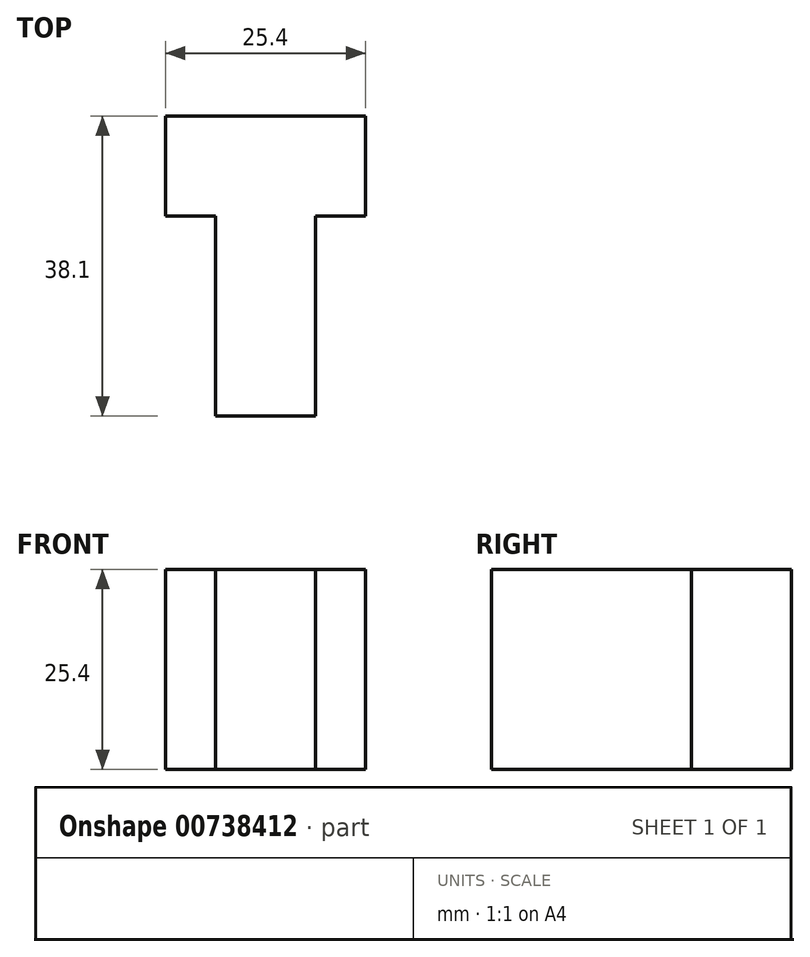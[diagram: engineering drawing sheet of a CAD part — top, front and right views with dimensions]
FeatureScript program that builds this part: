
annotation { "Feature Type Name" : "Feature", "Feature Type Description" : "" }
export const myFeature = defineFeature(function(context is Context, id is Id, definition is map)
    precondition{}
    {
        {
            var Q0;
            Q0=qCreatedBy(makeId("Top.planeOp"),FACE);
            var sketch = newSketch(context, id + "F0", { "sketchPlane" : qUnion([Q0])});
            skLineSegment(sketch, "E0", {"start": v(0, 17.79) * mm, "end": v(0, -7.61) * mm});
            skLineSegment(sketch, "E1", {"start": v(0, -7.61) * mm, "end": v(12.7, -7.61) * mm});
            skLineSegment(sketch, "E2", {"start": v(12.7, -7.61) * mm, "end": v(12.7, 17.79) * mm});
            skLineSegment(sketch, "E3", {"start": v(12.7, 17.79) * mm, "end": v(19.05, 17.79) * mm});
            skLineSegment(sketch, "E4", {"start": v(19.05, 17.79) * mm, "end": v(19.05, 30.49) * mm});
            skLineSegment(sketch, "E5", {"start": v(19.05, 30.49) * mm, "end": v(-6.35, 30.49) * mm});
            skLineSegment(sketch, "E6", {"start": v(-6.35, 30.49) * mm, "end": v(-6.35, 17.79) * mm});
            skLineSegment(sketch, "E7", {"start": v(-6.35, 17.79) * mm, "end": v(0, 17.79) * mm});
            skSolve(sketch);
        }
        {
            var Q0;
            Q0 = qSketchRegion(id + "F0", true);
            extrude(context, id + "F1", {"entities" : qUnion([Q0]), "depth" : 25.4 * mm, "offsetDistance" : 25.4 * mm});
        }
    });
